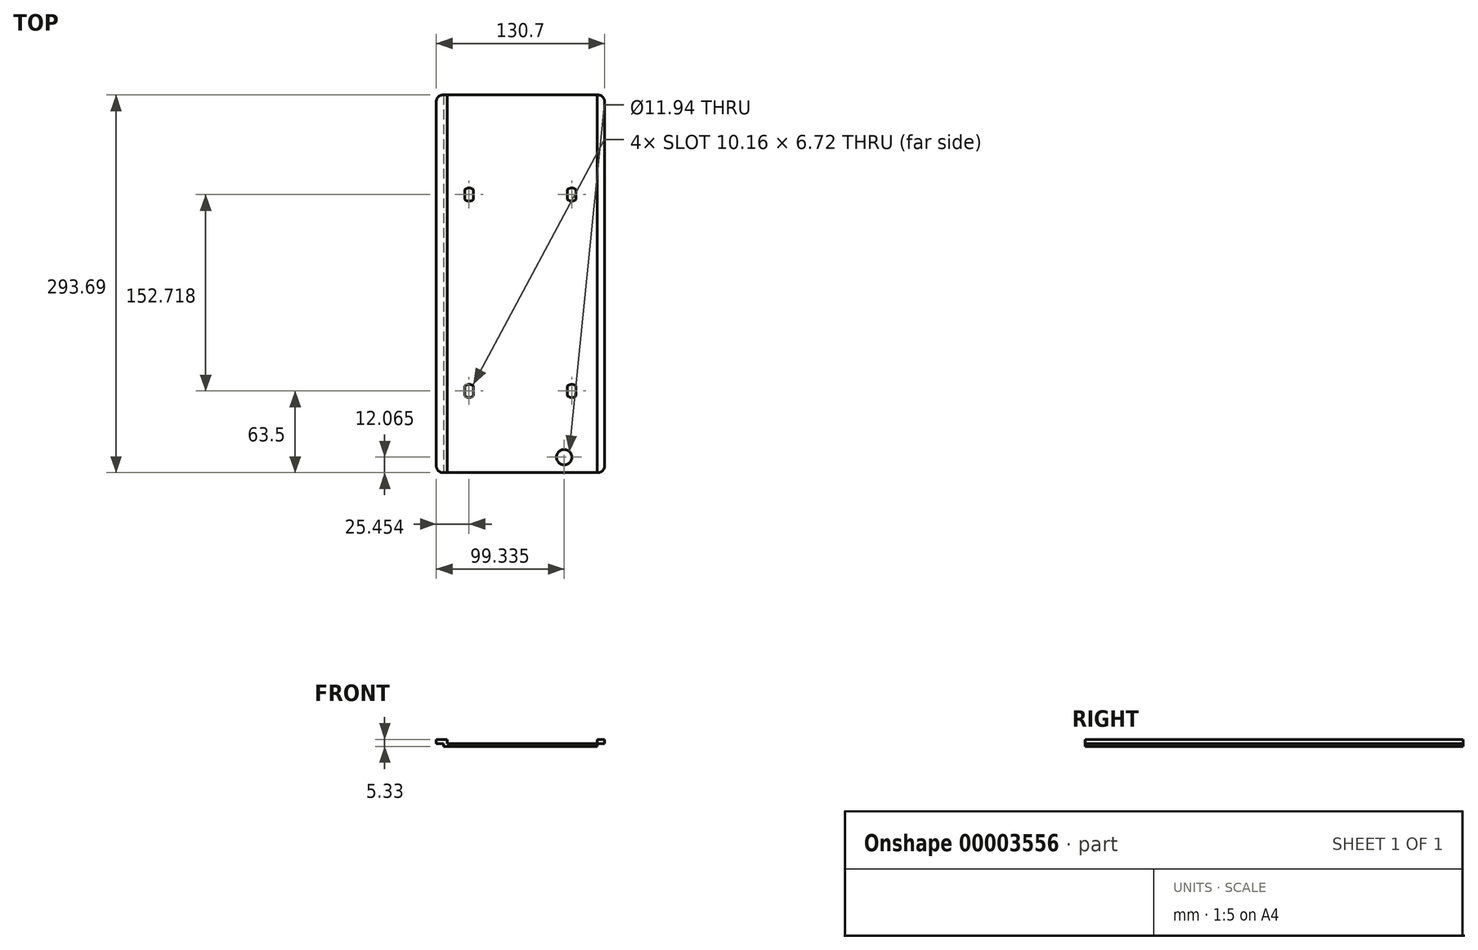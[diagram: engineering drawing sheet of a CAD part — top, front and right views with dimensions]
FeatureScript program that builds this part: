
annotation { "Feature Type Name" : "Feature", "Feature Type Description" : "" }
export const myFeature = defineFeature(function(context is Context, id is Id, definition is map)
    precondition{}
    {
        {
            var Q0;
            Q0=qCreatedBy(makeId("Front.planeOp"),FACE);
            var sketch = newSketch(context, id + "F0", { "sketchPlane" : qUnion([Q0])});
            skLineSegment(sketch, "E0.bottom", {"start": v(0, 0) * mm, "end": v(119.38, 0) * mm});
            skLineSegment(sketch, "E0.top", {"start": v(0, 2.16) * mm, "end": v(119.38, 2.16) * mm});
            skLineSegment(sketch, "E0.left", {"start": v(0, 0) * mm, "end": v(0, 2.16) * mm});
            skLineSegment(sketch, "E0.right", {"start": v(119.38, 0) * mm, "end": v(119.38, 2.16) * mm});
            skLineSegment(sketch, "E1", {"start": v(2.72, 2.16) * mm, "end": v(2.72, 5.33) * mm});
            skLineSegment(sketch, "E2", {"start": v(2.72, 5.33) * mm, "end": v(0, 5.33) * mm});
            skLineSegment(sketch, "E3", {"start": v(0, 5.33) * mm, "end": v(0, 2.16) * mm});
            skLineSegment(sketch, "E4.bottom", {"start": v(119.38, 2.16) * mm, "end": v(116.66, 2.16) * mm});
            skLineSegment(sketch, "E4.top", {"start": v(119.38, 5.33) * mm, "end": v(116.66, 5.33) * mm});
            skLineSegment(sketch, "E4.left", {"start": v(119.38, 2.16) * mm, "end": v(119.38, 5.33) * mm});
            skLineSegment(sketch, "E4.right", {"start": v(116.66, 2.16) * mm, "end": v(116.66, 5.33) * mm});
            skLineSegment(sketch, "E5.bottom", {"start": v(119.38, 5.33) * mm, "end": v(125.04, 5.33) * mm});
            skLineSegment(sketch, "E5.top", {"start": v(119.38, 2.16) * mm, "end": v(125.04, 2.16) * mm});
            skLineSegment(sketch, "E5.left", {"start": v(119.38, 5.33) * mm, "end": v(119.38, 2.16) * mm});
            skLineSegment(sketch, "E5.right", {"start": v(125.04, 5.33) * mm, "end": v(125.04, 2.16) * mm});
            skLineSegment(sketch, "E6.bottom", {"start": v(0, 5.33) * mm, "end": v(-5.66, 5.33) * mm});
            skLineSegment(sketch, "E6.top", {"start": v(0, 2.16) * mm, "end": v(-5.66, 2.16) * mm});
            skLineSegment(sketch, "E6.right", {"start": v(-5.66, 5.33) * mm, "end": v(-5.66, 2.16) * mm});
            skSolve(sketch);
        }
        {
            var Q0;
            Q0=makeQuery(id+"F0.imprint","IMPRINT",FACE,{"disambiguationData":[TD([[makeQuery(id+"F0.imprint","IMPRINT",EDGE,{"derivedFrom":sQuery(id+"F0.wireOp",EDGE,"E5.bottom")}),-1.0]])]});
            var Q1;
            Q1=makeQuery(id+"F0.imprint","IMPRINT",FACE,{"disambiguationData":[TD([[makeQuery(id+"F0.imprint","IMPRINT",EDGE,{"derivedFrom":sQuery(id+"F0.wireOp",EDGE,"E6.bottom")}),1.0]])]});
            var Q2;
            Q2=makeQuery(id+"F0.imprint","IMPRINT",FACE,{"disambiguationData":[TD([[makeQuery(id+"F0.imprint","IMPRINT",EDGE,{"derivedFrom":sQuery(id+"F0.wireOp",EDGE,"E0.bottom")}),1.0]])]});
            var Q3;
            {var subQ1=sQuery(id+"F0.wireOp",EDGE,"E1");Q3=makeQuery(id+"F0.imprint","IMPRINT",FACE,{"disambiguationData":[TD([[makeQuery(id+"F0.imprint","IMPRINT",EDGE,{"derivedFrom":subQ1}),1.0]])]});}
            var Q4;
            Q4=makeQuery(id+"F0.imprint","IMPRINT",FACE,{"disambiguationData":[TD([[makeQuery(id+"F0.imprint","IMPRINT",EDGE,{"derivedFrom":sQuery(id+"F0.wireOp",EDGE,"E4.bottom")}),-1.0]])]});
            extrude(context, id + "F1", {"entities" : qUnion([Q0, Q1, Q2, Q3, Q4]), "oppositeDirection" : true, "depth" : 293.7 * mm});
        }
        {
            var Q0;
            Q0=makeQuery(id+"F1.opExtrude","CAP_EDGE",EDGE,{"disambiguationData":[OSD([sQuery(id+"F0.wireOp",EDGE,"E5.right")])],"isStart":true});
            var Q1;
            Q1=makeQuery(id+"F1.opExtrude","CAP_EDGE",EDGE,{"disambiguationData":[OSD([sQuery(id+"F0.wireOp",EDGE,"E6.right")])],"isStart":true});
            var Q2;
            Q2=makeQuery(id+"F1.opExtrude","CAP_EDGE",EDGE,{"disambiguationData":[OSD([sQuery(id+"F0.wireOp",EDGE,"E5.right")])],"isStart":false});
            var Q3;
            Q3=makeQuery(id+"F1.opExtrude","CAP_EDGE",EDGE,{"disambiguationData":[OSD([sQuery(id+"F0.wireOp",EDGE,"E6.right")])],"isStart":false});
            fillet(context, id + "F2", {"entities" : qUnion([Q0, Q1, Q2, Q3]), "radius" : 5.08 * mm, "tangentPropagation" : true, "allowEdgeOverflow" : false});
        }
        {
            var Q0;
            Q0=makeQuery(id+"F1.opExtrude","SWEPT_FACE",FACE,{"disambiguationData":[OSD([sQuery(id+"F0.wireOp",EDGE,"E0.top")])]});
            var sketch = newSketch(context, id + "F3", { "sketchPlane" : qUnion([Q0])});
            skCircle(sketch, "E7", {"center": v(93.68, 12.06) * mm, "radius": 5.97 * mm});
            skSolve(sketch);
        }
        {
            var Q0;
            Q0=makeQuery(id+"F3.imprint","IMPRINT",FACE,{"disambiguationData":[TD([[makeQuery(id+"F3.imprint","IMPRINT",EDGE,{"derivedFrom":sQuery(id+"F3.wireOp",EDGE,"E7")}),1.0]])]});
            extrude(context, id + "F4", {"entities" : qUnion([Q0]), "operationType" : NewBodyOperationType.REMOVE, "endBound" : BoundingType.THROUGH_ALL, "oppositeDirection" : true, "depth" : 25.4 * mm});
        }
        {
            var Q0;
            Q0=makeQuery(id+"F1.opExtrude","SWEPT_FACE",FACE,{"disambiguationData":[OSD([sQuery(id+"F0.wireOp",EDGE,"E0.top")])]});
            var sketch = newSketch(context, id + "F5", { "sketchPlane" : qUnion([Q0])});
            skArc(sketch, "E8", {"start": v(16.43, 59.69) * mm, "mid": v(19.8, 58.42) * mm, "end": v(23.15, 59.69) * mm});
            skArc(sketch, "E9", {"start": v(96.23, 59.69) * mm, "mid": v(99.59, 58.42) * mm, "end": v(102.95, 59.69) * mm});
            skArc(sketch, "E10", {"start": v(96.23, 212.4) * mm, "mid": v(99.59, 211.14) * mm, "end": v(102.95, 212.4) * mm});
            skArc(sketch, "E11", {"start": v(16.43, 212.4) * mm, "mid": v(19.8, 211.14) * mm, "end": v(23.15, 212.4) * mm});
            skLineSegment(sketch, "E12", {"start": v(23.15, 59.69) * mm, "end": v(23.15, 67.3) * mm});
            skLineSegment(sketch, "E13", {"start": v(16.43, 67.31) * mm, "end": v(16.43, 59.69) * mm});
            skLineSegment(sketch, "E14", {"start": v(16.43, 212.4) * mm, "end": v(16.43, 220.03) * mm});
            skLineSegment(sketch, "E15", {"start": v(23.15, 212.4) * mm, "end": v(23.15, 220.03) * mm});
            skLineSegment(sketch, "E16", {"start": v(96.23, 212.4) * mm, "end": v(96.23, 220.03) * mm});
            skLineSegment(sketch, "E17", {"start": v(102.95, 212.4) * mm, "end": v(102.95, 220.03) * mm});
            skLineSegment(sketch, "E18", {"start": v(96.23, 59.69) * mm, "end": v(96.23, 67.31) * mm});
            skLineSegment(sketch, "E19", {"start": v(102.95, 59.69) * mm, "end": v(102.95, 67.31) * mm});
            skArc(sketch, "E20.trimOffspring", {"start": v(23.15, 67.3) * mm, "mid": v(19.8, 68.58) * mm, "end": v(16.43, 67.31) * mm});
            skArc(sketch, "E21.trimOffspring", {"start": v(23.15, 220.03) * mm, "mid": v(19.8, 221.3) * mm, "end": v(16.43, 220.03) * mm});
            skArc(sketch, "E22.trimOffspring", {"start": v(102.95, 220.03) * mm, "mid": v(99.59, 221.3) * mm, "end": v(96.23, 220.03) * mm});
            skArc(sketch, "E23.trimOffspring", {"start": v(102.95, 67.31) * mm, "mid": v(99.59, 68.58) * mm, "end": v(96.23, 67.3) * mm});
            skSolve(sketch);
        }
        {
            var Q0;
            Q0=makeQuery(id+"F5.imprint","IMPRINT",FACE,{"disambiguationData":[TD([[makeQuery(id+"F5.imprint","IMPRINT",EDGE,{"derivedFrom":sQuery(id+"F5.wireOp",EDGE,"E8")}),1.0]])]});
            var Q1;
            Q1=makeQuery(id+"F5.imprint","IMPRINT",FACE,{"disambiguationData":[TD([[makeQuery(id+"F5.imprint","IMPRINT",EDGE,{"derivedFrom":sQuery(id+"F5.wireOp",EDGE,"E9")}),1.0]])]});
            var Q2;
            Q2=makeQuery(id+"F5.imprint","IMPRINT",FACE,{"disambiguationData":[TD([[makeQuery(id+"F5.imprint","IMPRINT",EDGE,{"derivedFrom":sQuery(id+"F5.wireOp",EDGE,"E11")}),1.0]])]});
            var Q3;
            Q3=makeQuery(id+"F5.imprint","IMPRINT",FACE,{"disambiguationData":[TD([[makeQuery(id+"F5.imprint","IMPRINT",EDGE,{"derivedFrom":sQuery(id+"F5.wireOp",EDGE,"E10")}),1.0]])]});
            extrude(context, id + "F6", {"entities" : qUnion([Q0, Q1, Q2, Q3]), "operationType" : NewBodyOperationType.REMOVE, "endBound" : BoundingType.THROUGH_ALL, "oppositeDirection" : true, "depth" : 25.4 * mm});
        }
    });
